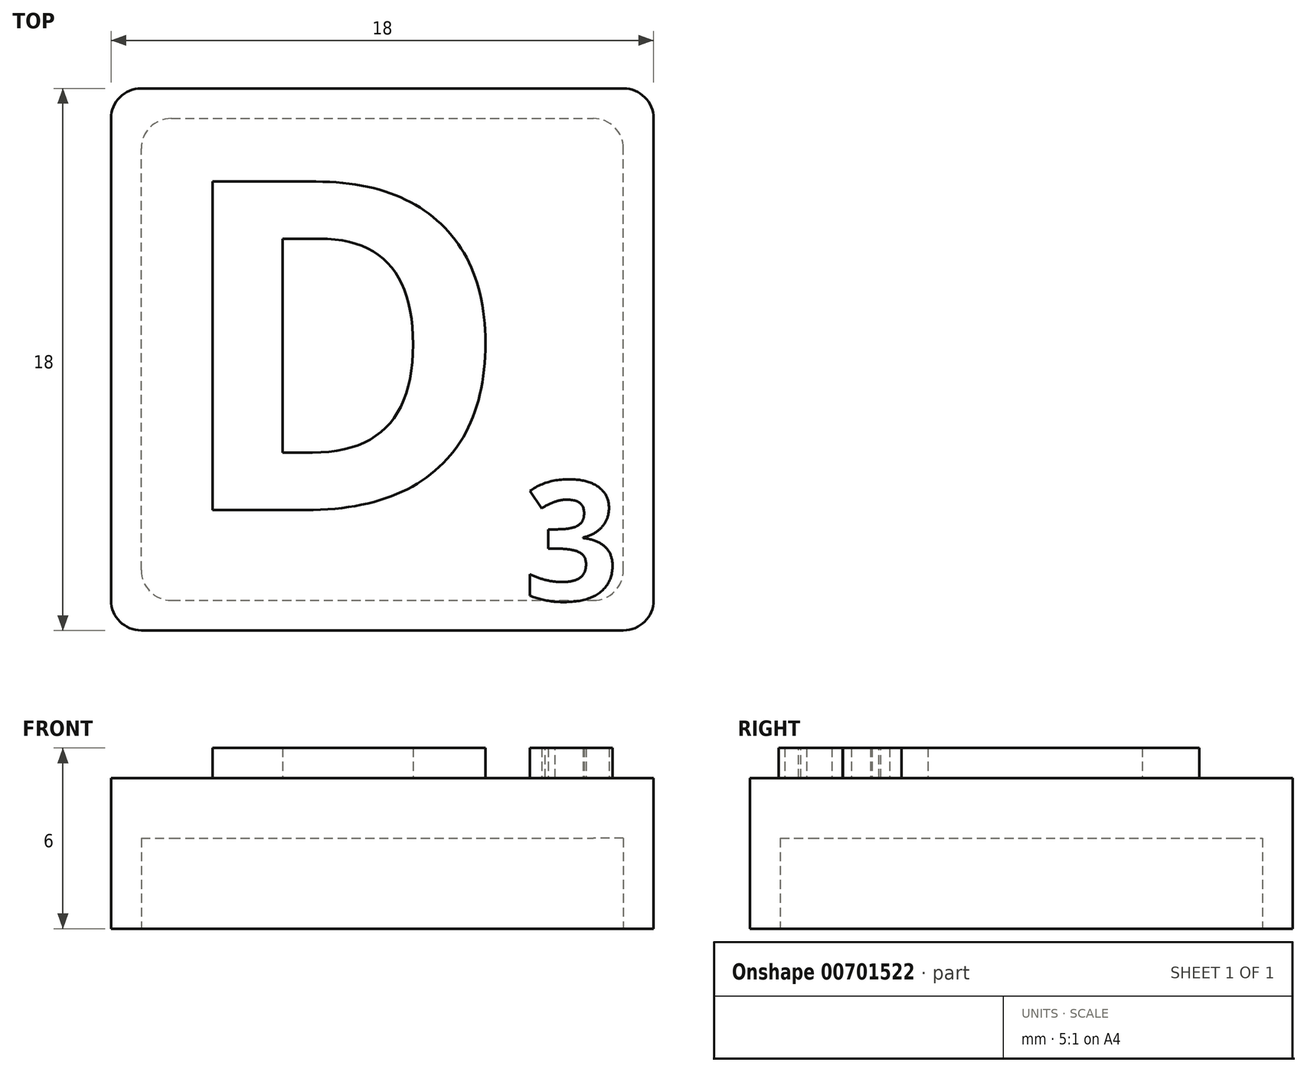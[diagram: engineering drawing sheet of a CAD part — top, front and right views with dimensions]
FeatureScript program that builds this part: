
annotation { "Feature Type Name" : "Feature", "Feature Type Description" : "" }
export const myFeature = defineFeature(function(context is Context, id is Id, definition is map)
    precondition{}
    {
        {
            var Q0;
            Q0=qCreatedBy(makeId("Top.planeOp"),FACE);
            var sketch = newSketch(context, id + "F0", { "sketchPlane" : qUnion([Q0])});
            skLineSegment(sketch, "E0.bottom", {"start": v(-3.93, 7.24) * mm, "end": v(14.07, 7.24) * mm});
            skLineSegment(sketch, "E0.top", {"start": v(-3.93, -10.76) * mm, "end": v(14.07, -10.76) * mm});
            skLineSegment(sketch, "E0.left", {"start": v(-3.93, 7.24) * mm, "end": v(-3.93, -10.76) * mm});
            skLineSegment(sketch, "E0.right", {"start": v(14.07, 7.24) * mm, "end": v(14.07, -10.76) * mm});
            skSolve(sketch);
        }
        {
            var Q0;
            Q0=qSketchRegion(id+"F0",true);
            extrude(context, id + "F1", {"entities" : qUnion([Q0]), "depth" : 5 * mm, "offsetDistance" : 25 * mm});
        }
        {
            var Q0;
            Q0=qCreatedBy(makeId("Top.planeOp"),FACE);
            var sketch = newSketch(context, id + "F2", { "sketchPlane" : qUnion([Q0])});
            skLineSegment(sketch, "E1.bottom", {"start": v(-2.93, -9.76) * mm, "end": v(13.07, -9.76) * mm});
            skLineSegment(sketch, "E1.top", {"start": v(-2.93, 6.24) * mm, "end": v(13.07, 6.24) * mm});
            skLineSegment(sketch, "E1.left", {"start": v(-2.93, -9.76) * mm, "end": v(-2.93, 6.24) * mm});
            skLineSegment(sketch, "E1.right", {"start": v(13.07, -9.76) * mm, "end": v(13.07, 6.24) * mm});
            skSolve(sketch);
        }
        {
            var Q0;
            Q0=makeQuery(id+"F2.imprint","IMPRINT",FACE,{"disambiguationData":[TD([[makeQuery(id+"F2.imprint","IMPRINT",EDGE,{"derivedFrom":sQuery(id+"F2.wireOp",EDGE,"E1.bottom")}),1.0]])]});
            extrude(context, id + "F3", {"entities" : qUnion([Q0]), "operationType" : NewBodyOperationType.REMOVE, "depth" : 3 * mm, "offsetDistance" : 25 * mm});
        }
        {
            var Q0;
            Q0=makeQuery(id+"F1.opExtrude","CAP_FACE",FACE,{"disambiguationData":[OSD([sQuery(id+"F0.wireOp",EDGE,"E0.bottom"),sQuery(id+"F0.wireOp",EDGE,"E0.top"),sQuery(id+"F0.wireOp",EDGE,"E0.left"),sQuery(id+"F0.wireOp",EDGE,"E0.right")])],"isStart":false});
            var sketch = newSketch(context, id + "F4", { "sketchPlane" : qUnion([Q0])});
            skText(sketch, "E2", { "text": "D", "fontName": "OpenSans-Bold.ttf"});
            skText(sketch, "E3", { "text": "3", "fontName": "OpenSans-Bold.ttf"});
            const initialGuessF4  = {"E2": [-0.00193, -0.00676, 1, 0, 0.011], "E3": [0.00975, -0.00976, 1, 0, 0.004]};
            skSetInitialGuess(sketch, initialGuessF4);
            skSolve(sketch);
        }
        {
            var Q0;
            Q0=makeQuery(id+"F4.imprint","IMPRINT",FACE,{"disambiguationData":[TD([[makeQuery(id+"F4.imprint","IMPRINT",EDGE,{"derivedFrom":sQuery(id+"F4.wireOp",EDGE,"E2.sketch_text.stroke-0")}),-1.0]])]});
            var Q1;
            Q1=makeQuery(id+"F4.imprint","IMPRINT",FACE,{"disambiguationData":[TD([[makeQuery(id+"F4.imprint","IMPRINT",EDGE,{"derivedFrom":sQuery(id+"F4.wireOp",EDGE,"E3.sketch_text.stroke-0")}),-1.0]])]});
            var Q2;
            Q2=makeQuery(id+"F4.imprint","IMPRINT",FACE,{"disambiguationData":[TD([[makeQuery(id+"F4.imprint","IMPRINT",EDGE,{"derivedFrom":sQuery(id+"F4.wireOp",EDGE,"E3.sketch_text.stroke-10")}),-1.0]])]});
            extrude(context, id + "F5", {"entities" : qUnion([Q0, Q1, Q2]), "operationType" : NewBodyOperationType.ADD, "depth" : 1 * mm, "offsetDistance" : 25 * mm});
        }
        {
            var Q0;
            Q0=makeQuery(id+"F1.opExtrude","SWEPT_EDGE",EDGE,{"disambiguationData":[OSD([sQuery(id+"F0.wireOp",EDGE,"E0.bottom"),sQuery(id+"F0.wireOp",EDGE,"E0.right")])]});
            var Q1;
            Q1=makeQuery(id+"F1.opExtrude","SWEPT_EDGE",EDGE,{"disambiguationData":[OSD([sQuery(id+"F0.wireOp",EDGE,"E0.top"),sQuery(id+"F0.wireOp",EDGE,"E0.right")])]});
            var Q2;
            Q2=makeQuery(id+"F1.opExtrude","SWEPT_EDGE",EDGE,{"disambiguationData":[OSD([sQuery(id+"F0.wireOp",EDGE,"E0.top"),sQuery(id+"F0.wireOp",EDGE,"E0.left")])]});
            var Q3;
            Q3=makeQuery(id+"F1.opExtrude","SWEPT_EDGE",EDGE,{"disambiguationData":[OSD([sQuery(id+"F0.wireOp",EDGE,"E0.bottom"),sQuery(id+"F0.wireOp",EDGE,"E0.left")])]});
            var Q4;
            Q4=makeQuery(id+"F3.boolean.opBoolean","COPY",EDGE,{"derivedFrom":makeQuery(id+"F3.opExtrude","SWEPT_EDGE",EDGE,{"disambiguationData":[OSD([sQuery(id+"F2.wireOp",EDGE,"E1.bottom"),sQuery(id+"F2.wireOp",EDGE,"E1.right")])]})});
            var Q5;
            Q5=makeQuery(id+"F3.boolean.opBoolean","COPY",EDGE,{"derivedFrom":makeQuery(id+"F3.opExtrude","SWEPT_EDGE",EDGE,{"disambiguationData":[OSD([sQuery(id+"F2.wireOp",EDGE,"E1.bottom"),sQuery(id+"F2.wireOp",EDGE,"E1.left")])]})});
            var Q6;
            Q6=makeQuery(id+"F3.boolean.opBoolean","COPY",EDGE,{"derivedFrom":makeQuery(id+"F3.opExtrude","SWEPT_EDGE",EDGE,{"disambiguationData":[OSD([sQuery(id+"F2.wireOp",EDGE,"E1.top"),sQuery(id+"F2.wireOp",EDGE,"E1.left")])]})});
            var Q7;
            Q7=makeQuery(id+"F3.boolean.opBoolean","COPY",EDGE,{"derivedFrom":makeQuery(id+"F3.opExtrude","SWEPT_EDGE",EDGE,{"disambiguationData":[OSD([sQuery(id+"F2.wireOp",EDGE,"E1.top"),sQuery(id+"F2.wireOp",EDGE,"E1.right")])]})});
            fillet(context, id + "F6", {"entities" : qUnion([Q0, Q1, Q2, Q3, Q4, Q5, Q6, Q7]), "radius" : 1 * mm, "tangentPropagation" : true, "allowEdgeOverflow" : false});
        }
    });
